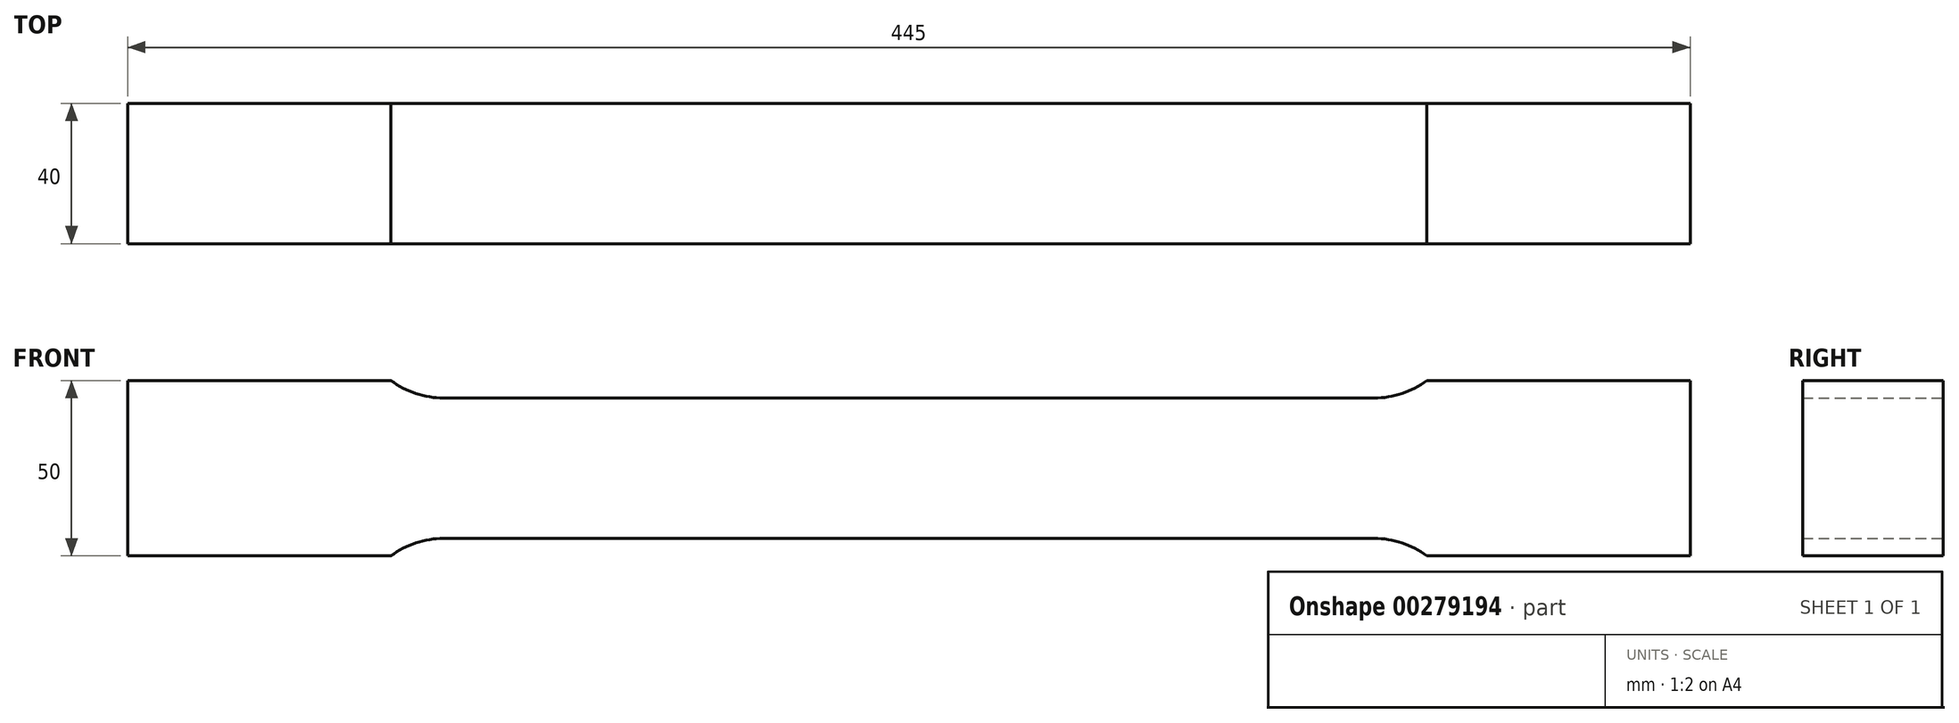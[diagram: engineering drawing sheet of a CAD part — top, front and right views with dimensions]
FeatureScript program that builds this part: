
annotation { "Feature Type Name" : "Feature", "Feature Type Description" : "" }
export const myFeature = defineFeature(function(context is Context, id is Id, definition is map)
    precondition{}
    {
        {
            var Q0;
            Q0=qCreatedBy(makeId("Front.planeOp"),FACE);
            var sketch = newSketch(context, id + "F0", { "sketchPlane" : qUnion([Q0])});
            skLineSegment(sketch, "E0", {"start": v(0, 20) * mm, "end": v(132.5, 20) * mm});
            skArc(sketch, "E1", {"start": v(132.5, 20) * mm, "mid": v(140.4, 21.28) * mm, "end": v(147.5, 25) * mm});
            skLineSegment(sketch, "E2", {"start": v(147.5, 25) * mm, "end": v(222.5, 25) * mm});
            skLineSegment(sketch, "E3", {"start": v(222.5, 25) * mm, "end": v(222.5, 0) * mm});
            skLineSegment(sketch, "E4.MirrorCS", {"start": v(0, -20) * mm, "end": v(132.5, -20) * mm});
            skLineSegment(sketch, "E5.MirrorCS", {"start": v(147.5, -25) * mm, "end": v(222.5, -25) * mm});
            skLineSegment(sketch, "E6.MirrorCS", {"start": v(222.5, -25) * mm, "end": v(222.5, 0) * mm});
            skArc(sketch, "E7.MirrorCS", {"start": v(132.5, -20) * mm, "mid": v(140.4, -21.28) * mm, "end": v(147.5, -25) * mm});
            skArc(sketch, "E8.MirrorCS", {"start": v(-132.5, -20) * mm, "mid": v(-140.4, -21.28) * mm, "end": v(-147.5, -25) * mm});
            skLineSegment(sketch, "E9.MirrorCS", {"start": v(-222.5, -25) * mm, "end": v(-222.5, 0) * mm});
            skLineSegment(sketch, "E10.MirrorCS", {"start": v(0, 20) * mm, "end": v(-132.5, 20) * mm});
            skArc(sketch, "E11.MirrorCS", {"start": v(-132.5, 20) * mm, "mid": v(-140.4, 21.28) * mm, "end": v(-147.5, 25) * mm});
            skLineSegment(sketch, "E12.MirrorCS", {"start": v(-147.5, 25) * mm, "end": v(-222.5, 25) * mm});
            skLineSegment(sketch, "E13.MirrorCS", {"start": v(-147.5, -25) * mm, "end": v(-222.5, -25) * mm});
            skLineSegment(sketch, "E14.MirrorCS", {"start": v(-222.5, 25) * mm, "end": v(-222.5, 0) * mm});
            skLineSegment(sketch, "E15.MirrorCS", {"start": v(0, -20) * mm, "end": v(-132.5, -20) * mm});
            skSolve(sketch);
        }
        {
            var Q0;
            Q0 = qSketchRegion(id + "F0", true);
            extrude(context, id + "F1", {"entities" : qUnion([Q0]), "endBound" : BoundingType.SYMMETRIC, "depth" : 40 * mm});
        }
    });
